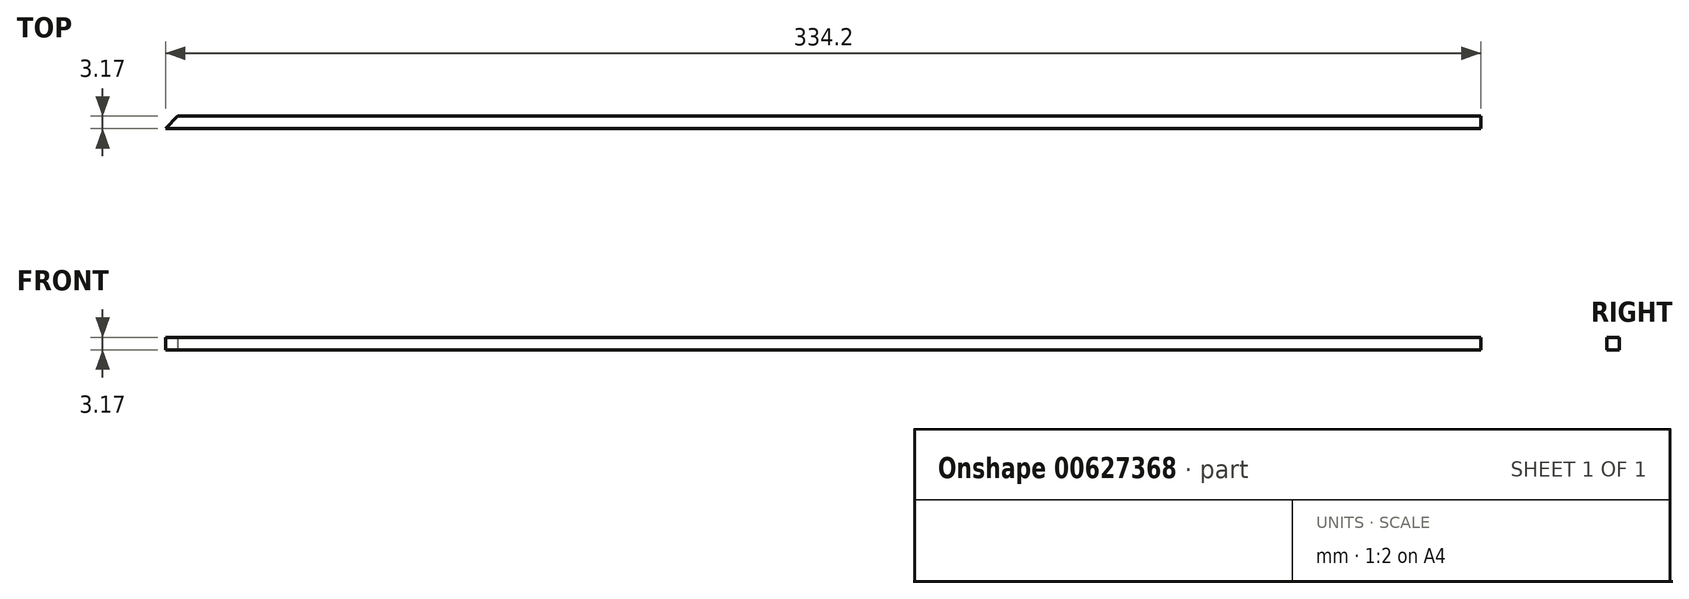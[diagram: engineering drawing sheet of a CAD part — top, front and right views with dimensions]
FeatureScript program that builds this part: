
annotation { "Feature Type Name" : "Feature", "Feature Type Description" : "" }
export const myFeature = defineFeature(function(context is Context, id is Id, definition is map)
    precondition{}
    {
        {
            var Q0;
            Q0=qCreatedBy(makeId("Top.planeOp"),FACE);
            var sketch = newSketch(context, id + "F0", { "sketchPlane" : qUnion([Q0])});
            skLineSegment(sketch, "E0", {"start": v(-141.7, 5.15) * mm, "end": v(189.4, 5.15) * mm});
            skLineSegment(sketch, "E1", {"start": v(189.4, 5.15) * mm, "end": v(189.4, 1.98) * mm});
            skLineSegment(sketch, "E2", {"start": v(189.4, 1.98) * mm, "end": v(-144.8, 1.98) * mm});
            skLineSegment(sketch, "E3", {"start": v(-144.8, 1.98) * mm, "end": v(-141.7, 5.15) * mm});
            skSolve(sketch);
        }
        {
            var Q0;
            Q0 = qSketchRegion(id + "F0", true);
            extrude(context, id + "F1", {"entities" : qUnion([Q0]), "depth" : 3.17 * mm, "offsetDistance" : 25.4 * mm});
        }
    });
